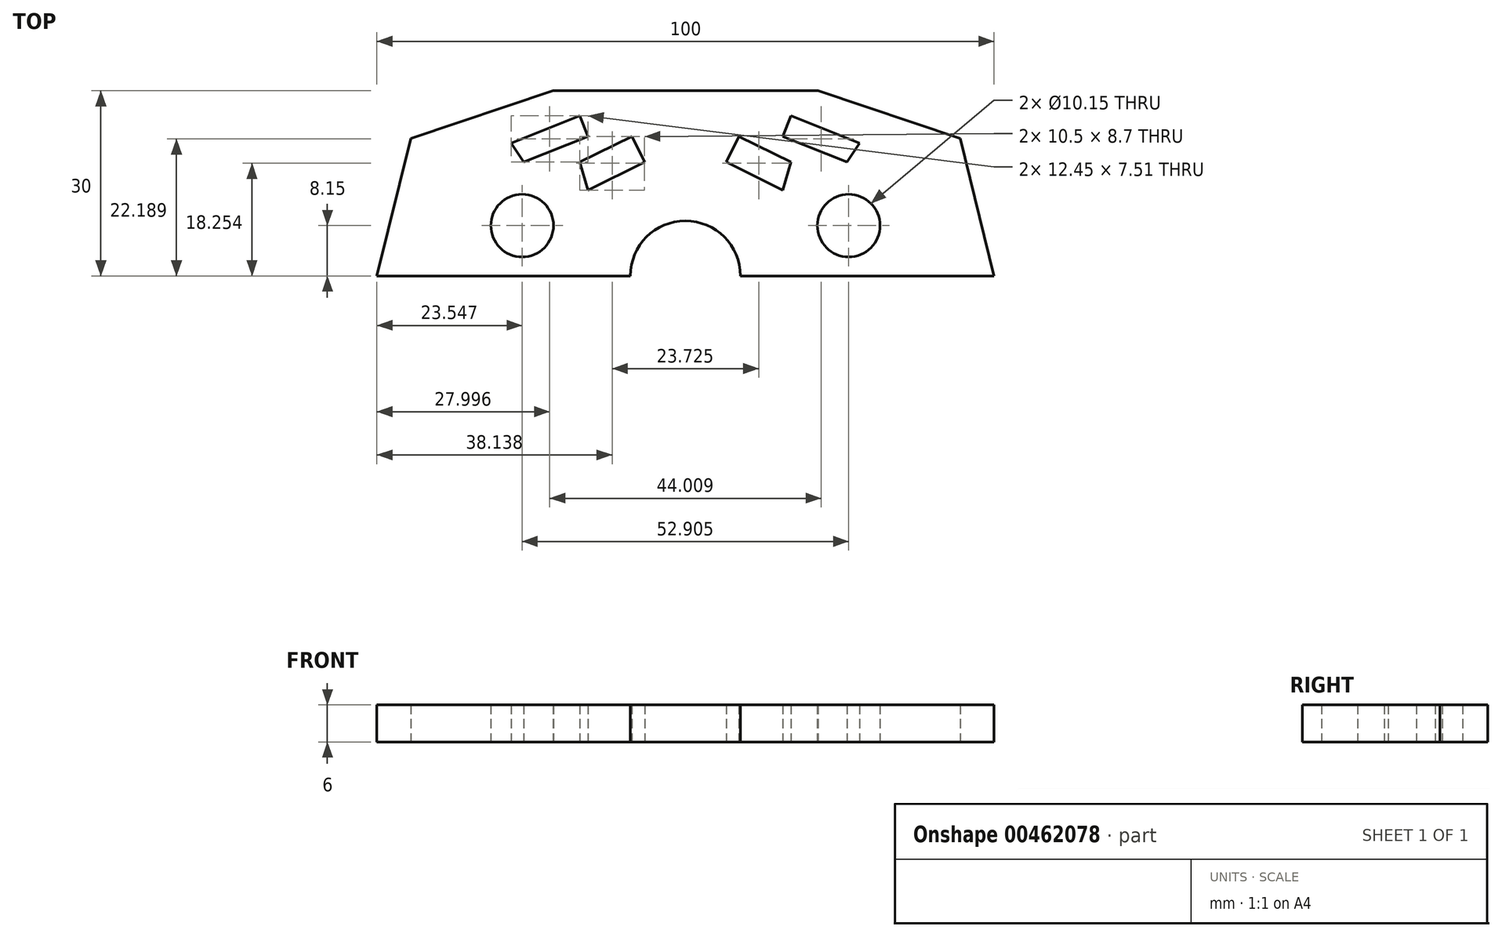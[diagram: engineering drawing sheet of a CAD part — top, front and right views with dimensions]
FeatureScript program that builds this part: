
annotation { "Feature Type Name" : "Feature", "Feature Type Description" : "" }
export const myFeature = defineFeature(function(context is Context, id is Id, definition is map)
    precondition{}
    {
        {
            var Q0;
            Q0=qCreatedBy(makeId("Top.planeOp"),FACE);
            var sketch = newSketch(context, id + "F0", { "sketchPlane" : qUnion([Q0])});
            skLineSegment(sketch, "E0", {"start": v(-50, 0) * mm, "end": v(0, 0) * mm});
            skLineSegment(sketch, "E1", {"start": v(0, 0) * mm, "end": v(0, 30) * mm});
            skLineSegment(sketch, "E2", {"start": v(0, 30) * mm, "end": v(-21.47, 30) * mm});
            skLineSegment(sketch, "E3", {"start": v(-21.47, 30) * mm, "end": v(-44.52, 22.26) * mm});
            skLineSegment(sketch, "E4", {"start": v(-44.52, 22.26) * mm, "end": v(-50, 0) * mm});
            skCircle(sketch, "E5", {"center": v(-26.45, 8.15) * mm, "radius": 5.08 * mm});
            skArc(sketch, "E6", {"start": v(0, 8.91) * mm, "mid": v(-6.3, 6.3) * mm, "end": v(-8.91, 0) * mm});
            skLineSegment(sketch, "E7", {"start": v(-28.23, 21.5) * mm, "end": v(-17.11, 25.94) * mm});
            skLineSegment(sketch, "E8", {"start": v(-17.11, 25.94) * mm, "end": v(-15.78, 22.6) * mm});
            skLineSegment(sketch, "E9", {"start": v(-15.78, 22.6) * mm, "end": v(-26.2, 18.43) * mm});
            skLineSegment(sketch, "E10", {"start": v(-26.2, 18.43) * mm, "end": v(-28.23, 21.5) * mm});
            skLineSegment(sketch, "E11", {"start": v(-17.11, 18.43) * mm, "end": v(-8.68, 22.6) * mm});
            skLineSegment(sketch, "E12", {"start": v(-8.68, 22.6) * mm, "end": v(-6.61, 18.43) * mm});
            skLineSegment(sketch, "E13", {"start": v(-6.61, 18.43) * mm, "end": v(-15.78, 13.9) * mm});
            skLineSegment(sketch, "E14", {"start": v(-15.78, 13.9) * mm, "end": v(-17.11, 18.43) * mm});
            skPoint(sketch, "E15.MirrorCS.end.orphan", {"position": v(21.47, 30) * mm});
            skPoint(sketch, "E15.MirrorCS.start.orphan", {"position": v(0, 30) * mm});
            skPoint(sketch, "E16.MirrorCS.end.orphan", {"position": v(44.52, 22.26) * mm});
            skPoint(sketch, "E17.MirrorCS.end.orphan", {"position": v(50, 0) * mm});
            skLineSegment(sketch, "E18.MirrorCS", {"start": v(0, 30) * mm, "end": v(21.47, 30) * mm});
            skLineSegment(sketch, "E19.MirrorCS", {"start": v(21.47, 30) * mm, "end": v(44.52, 22.26) * mm});
            skLineSegment(sketch, "E20.MirrorCS", {"start": v(44.52, 22.26) * mm, "end": v(50, 0) * mm});
            skLineSegment(sketch, "E21.MirrorCS", {"start": v(50, 0) * mm, "end": v(0, 0) * mm});
            skCircle(sketch, "E22.MirrorC", {"center": v(26.45, 8.15) * mm, "radius": 5.08 * mm});
            skLineSegment(sketch, "E23.MirrorCS", {"start": v(28.23, 21.5) * mm, "end": v(17.11, 25.94) * mm});
            skLineSegment(sketch, "E24.MirrorCS", {"start": v(26.2, 18.43) * mm, "end": v(28.23, 21.5) * mm});
            skLineSegment(sketch, "E25.MirrorCS", {"start": v(15.78, 22.6) * mm, "end": v(26.2, 18.43) * mm});
            skLineSegment(sketch, "E26.MirrorCS", {"start": v(15.78, 13.9) * mm, "end": v(17.11, 18.43) * mm});
            skLineSegment(sketch, "E27.MirrorCS", {"start": v(17.11, 18.43) * mm, "end": v(8.68, 22.6) * mm});
            skLineSegment(sketch, "E28.MirrorCS", {"start": v(6.61, 18.43) * mm, "end": v(15.78, 13.9) * mm});
            skLineSegment(sketch, "E29.MirrorCS", {"start": v(8.68, 22.6) * mm, "end": v(6.61, 18.43) * mm});
            skArc(sketch, "E30.MirrorCS", {"start": v(0, 8.91) * mm, "mid": v(6.3, 6.3) * mm, "end": v(8.91, 0) * mm});
            skLineSegment(sketch, "E31.MirrorCS", {"start": v(17.11, 25.94) * mm, "end": v(15.78, 22.6) * mm});
            skSolve(sketch);
        }
        {
            var Q0;
            {var subQ3=sQuery(id+"F0.wireOp",EDGE,"E2");Q0=makeQuery(id+"F0.imprint","IMPRINT",FACE,{"disambiguationData":[TD([[makeQuery(id+"F0.imprint","IMPRINT",EDGE,{"derivedFrom":subQ3}),1.0]])]});}
            var Q1;
            {var subQ0=sQuery(id+"F0.wireOp",EDGE,"E18.MirrorCS");Q1=makeQuery(id+"F0.imprint","IMPRINT",FACE,{"disambiguationData":[TD([[makeQuery(id+"F0.imprint","IMPRINT",EDGE,{"derivedFrom":subQ0}),-1.0]])]});}
            extrude(context, id + "F1", {"entities" : qUnion([Q0, Q1]), "depth" : 6 * mm});
        }
    });
